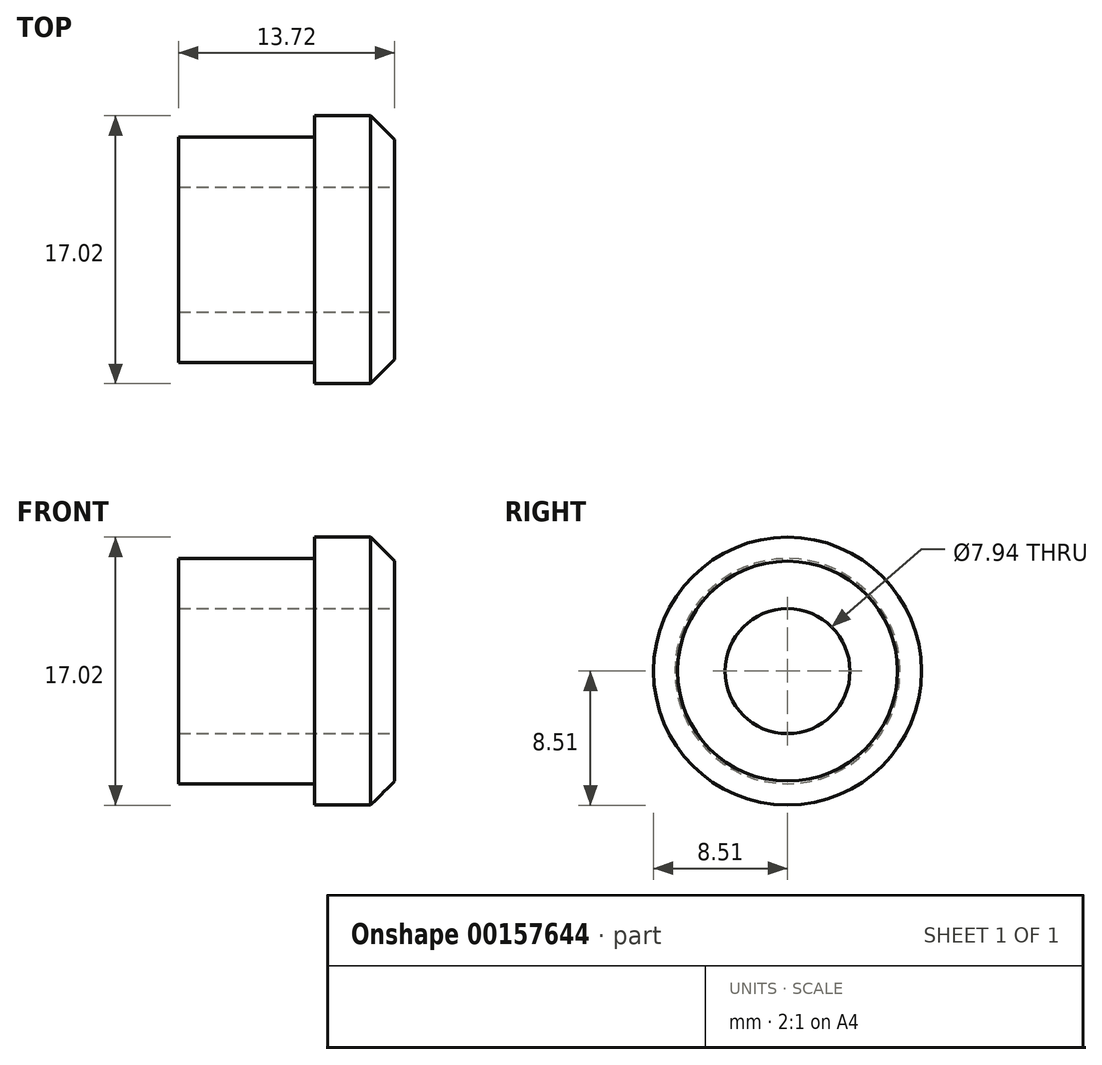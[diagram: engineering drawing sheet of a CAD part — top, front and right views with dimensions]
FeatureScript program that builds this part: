
annotation { "Feature Type Name" : "Feature", "Feature Type Description" : "" }
export const myFeature = defineFeature(function(context is Context, id is Id, definition is map)
    precondition{}
    {
        {
            var Q0;
            Q0=qCreatedBy(makeId("Right.planeOp"),FACE);
            var sketch = newSketch(context, id + "F0", { "sketchPlane" : qUnion([Q0])});
            skCircle(sketch, "E0", {"center": v(0, 0) * mm, "radius": 3.97 * mm});
            skCircle(sketch, "E1", {"center": v(0, 0) * mm, "radius": 7.15 * mm});
            skCircle(sketch, "E2", {"center": v(0, 0) * mm, "radius": 8.5 * mm});
            skSolve(sketch);
        }
        {
            var Q0;
            Q0=makeQuery(id+"F0.imprint","IMPRINT",FACE,{"disambiguationData":[TD([[makeQuery(id+"F0.imprint","IMPRINT",EDGE,{"derivedFrom":sQuery(id+"F0.wireOp",EDGE,"E0")}),-1.0]])]});
            extrude(context, id + "F1", {"entities" : qUnion([Q0]), "oppositeDirection" : true, "depth" : 13.72 * mm});
        }
        {
            var Q0;
            Q0=makeQuery(id+"F0.imprint","IMPRINT",FACE,{"disambiguationData":[TD([[makeQuery(id+"F0.imprint","IMPRINT",EDGE,{"derivedFrom":sQuery(id+"F0.wireOp",EDGE,"E1")}),-1.0]])]});
            extrude(context, id + "F2", {"entities" : qUnion([Q0]), "operationType" : NewBodyOperationType.ADD, "oppositeDirection" : true, "depth" : 5.08 * mm});
        }
        {
            var Q0;
            Q0=makeQuery(id+"F2.opExtrude","CAP_EDGE",EDGE,{"disambiguationData":[OSD([sQuery(id+"F0.wireOp",EDGE,"E2")])],"isStart":true});
            chamfer(context, id + "F3", {"entities" : qUnion([Q0]), "width" : 1.52 * mm, "tangentPropagation" : true});
        }
    });
